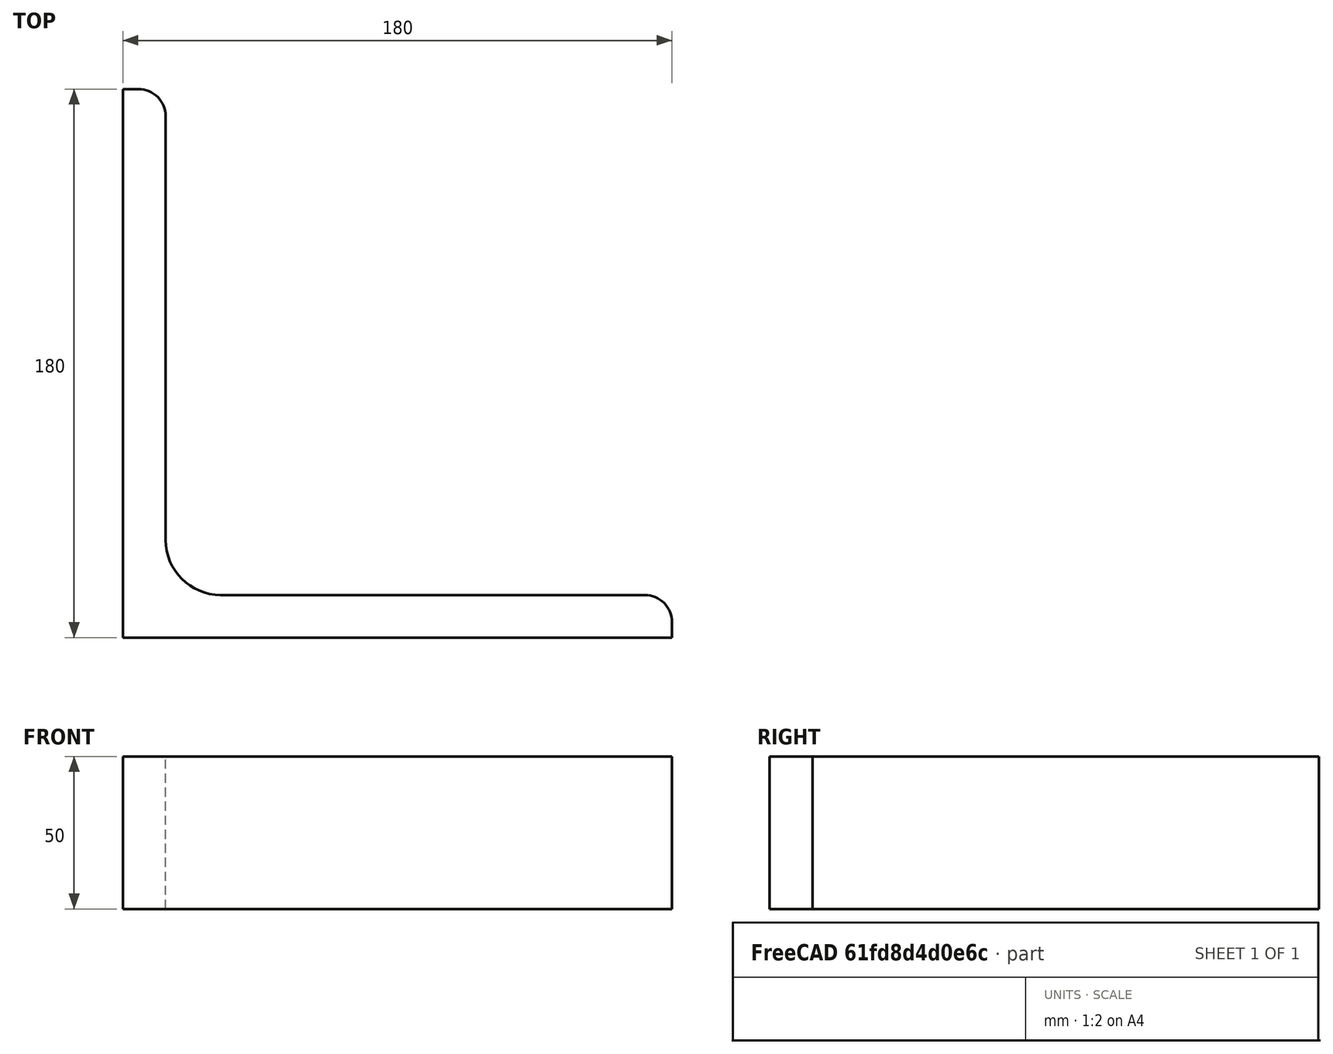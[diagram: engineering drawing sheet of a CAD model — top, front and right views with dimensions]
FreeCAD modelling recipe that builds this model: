
FCSTD DOCUMENT  (FreeCAD 0.15R4671 (Git))
Label: Angle Bar L180x180x14 EN10056 S235JR
License: All rights reserved
LicenseURL: http://en.wikipedia.org/wiki/All_rights_reserved
objects: Sketcher::SketchObject×1, Part::Extrusion×1
note: 2 computed .brp shape members not serialized (recipe doc carries the construction recipe); baked Part::Feature solids carry a one-line shape summary decoded from their .brp

FEATURE [Sketcher::SketchObject] Sketch
  sketch-geometry (9):
    g0: LineSegment StartX=0 StartY=0 StartZ=0 EndX=180 EndY=0 EndZ=0
    g1: LineSegment StartX=180 StartY=0 StartZ=0 EndX=180 EndY=5 EndZ=0
    g2: LineSegment StartX=171 StartY=14 StartZ=0 EndX=32 EndY=14 EndZ=0
    g3: LineSegment StartX=0 StartY=0 StartZ=0 EndX=0 EndY=180 EndZ=0
    g4: LineSegment StartX=0 StartY=180 StartZ=0 EndX=5 EndY=180 EndZ=0
    g5: LineSegment StartX=14 StartY=171 StartZ=0 EndX=14 EndY=32 EndZ=0
    g6: ArcOfCircle CenterX=32 CenterY=32 CenterZ=0 NormalX=0 NormalY=0 NormalZ=1 Radius=18 StartAngle=3.14159 EndAngle=4.71239
    g7: ArcOfCircle CenterX=5 CenterY=171 CenterZ=0 NormalX=0 NormalY=0 NormalZ=1 Radius=9 StartAngle=0 EndAngle=1.5708
    g8: ArcOfCircle CenterX=171 CenterY=5 CenterZ=0 NormalX=0 NormalY=0 NormalZ=1 Radius=9 StartAngle=0 EndAngle=1.5708
  constraints (23):
    c: Coincident(g0,g-1)
    c: Horizontal(g0)
    c: Coincident(g1,g0)
    c: Vertical(g1)
    c: Horizontal(g2)
    c: Coincident(g3,g-1)
    c: Vertical(g3)
    c: Coincident(g4,g3)
    c: Horizontal(g4)
    c: Vertical(g5)
    c: Tangent(g5,g6) = -1.5708
    c: Tangent(g2,g6) = 1.5708
    c: Tangent(g4,g7) = 1.5708
    c: Tangent(g5,g7) = 1.5708
    c: Tangent(g2,g8) = -1.5708
    c: Tangent(g1,g8) = -1.5708
    c: DistanceX(g0) = 180
    c: DistanceY(g3) = 180
    c: DistanceY(g0,g2) = 14
    c: DistanceX(g3,g5) = 14
    c: Radius(g6) = 18
    c: Radius(g8) = 9
    c: Radius(g7) = 9
FEATURE [Part::Extrusion] Extrude  label="Angle Bar L180x180x14 EN10056 S235JR"
  Base = -> Sketch
  Dir = (0,0,50)
  Solid = true
